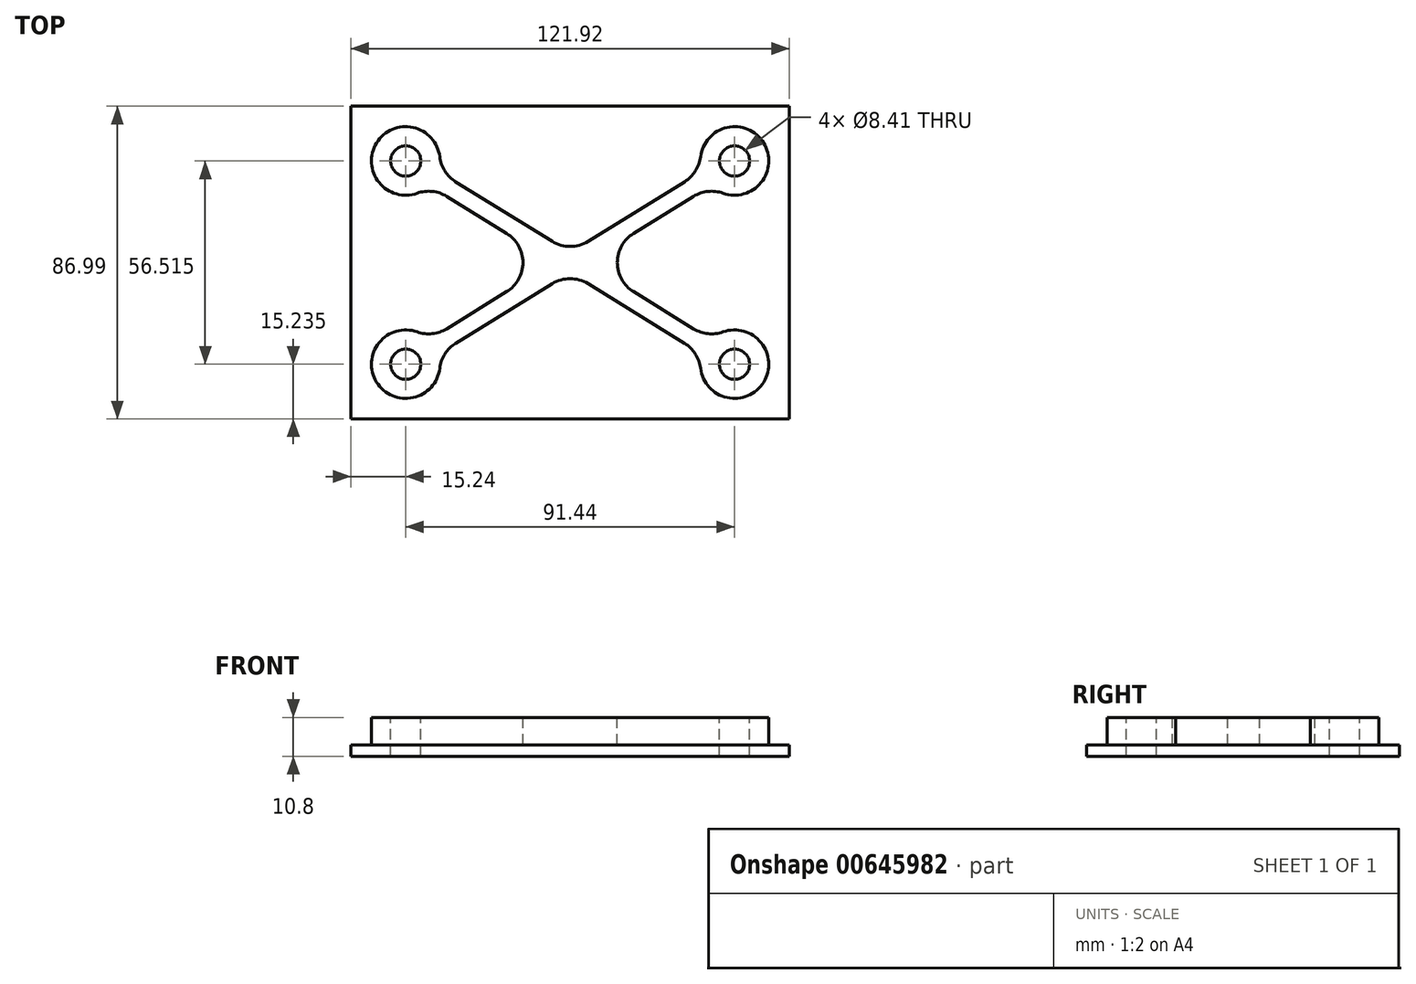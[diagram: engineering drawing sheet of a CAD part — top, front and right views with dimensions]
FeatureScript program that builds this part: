
annotation { "Feature Type Name" : "Feature", "Feature Type Description" : "" }
export const myFeature = defineFeature(function(context is Context, id is Id, definition is map)
    precondition{}
    {
        {
            var Q0;
            Q0=qCreatedBy(makeId("Top.planeOp"),FACE);
            var sketch = newSketch(context, id + "F0", { "sketchPlane" : qUnion([Q0])});
            skCircle(sketch, "E0", {"center": v(0, 0) * mm, "radius": 15.24 * mm});
            skCircle(sketch, "E1", {"center": v(-91.44, 0) * mm, "radius": 15.24 * mm});
            skCircle(sketch, "E2", {"center": v(0, -56.52) * mm, "radius": 15.24 * mm});
            skCircle(sketch, "E3", {"center": v(-91.44, -56.52) * mm, "radius": 15.24 * mm});
            skLineSegment(sketch, "E4", {"start": v(-106.68, 0) * mm, "end": v(-106.68, -56.52) * mm});
            skLineSegment(sketch, "E5", {"start": v(-91.44, -71.76) * mm, "end": v(0, -71.76) * mm});
            skLineSegment(sketch, "E6", {"start": v(15.24, 0) * mm, "end": v(15.24, -56.52) * mm});
            skLineSegment(sketch, "E7", {"start": v(0, 15.24) * mm, "end": v(-91.44, 15.24) * mm});
            skLineSegment(sketch, "E8", {"start": v(0, 15.24) * mm, "end": v(15.24, 15.24) * mm});
            skLineSegment(sketch, "E9", {"start": v(15.24, 0) * mm, "end": v(15.24, 15.24) * mm});
            skLineSegment(sketch, "E10", {"start": v(-91.44, 15.24) * mm, "end": v(-106.68, 15.24) * mm});
            skLineSegment(sketch, "E11", {"start": v(-106.68, 0) * mm, "end": v(-106.68, 15.24) * mm});
            skLineSegment(sketch, "E12", {"start": v(15.24, -56.52) * mm, "end": v(15.24, -71.76) * mm});
            skLineSegment(sketch, "E13", {"start": v(0, -71.76) * mm, "end": v(15.24, -71.76) * mm});
            skLineSegment(sketch, "E14", {"start": v(-106.68, -56.52) * mm, "end": v(-106.68, -71.76) * mm});
            skLineSegment(sketch, "E15", {"start": v(-91.44, -71.76) * mm, "end": v(-106.68, -71.76) * mm});
            skSolve(sketch);
        }
        {
            var Q0;
            {var subQ0=sQuery(id+"F0.wireOp",EDGE,"E4");Q0=makeQuery(id+"F0.imprint","IMPRINT",FACE,{"disambiguationData":[TD([[makeQuery(id+"F0.imprint","IMPRINT",EDGE,{"derivedFrom":subQ0}),1.0]])]});}
            var Q1;
            {var subQ0=sQuery(id+"F0.wireOp",EDGE,"E3");var subQ1=makeQuery(id+"F0.imprint","INTERSECT",VERTEX,{"derivedFrom":[subQ0,sQuery(id+"F0.wireOp",EDGE,"E4")]});Q1=makeQuery(id+"F0.imprint","IMPRINT",FACE,{"disambiguationData":[TD([[makeQuery(id+"F0.imprint","IMPRINT",EDGE,{"disambiguationData":[TD([[subQ1,-1.0]])],"derivedFrom":subQ0}),1.0]])]});}
            var Q2;
            {var subQ0=sQuery(id+"F0.wireOp",EDGE,"E1");var subQ1=makeQuery(id+"F0.imprint","INTERSECT",VERTEX,{"derivedFrom":[subQ0,sQuery(id+"F0.wireOp",EDGE,"E4")]});Q2=makeQuery(id+"F0.imprint","IMPRINT",FACE,{"disambiguationData":[TD([[makeQuery(id+"F0.imprint","IMPRINT",EDGE,{"disambiguationData":[TD([[subQ1,1.0]])],"derivedFrom":subQ0}),1.0]])]});}
            var Q3;
            {var subQ0=sQuery(id+"F0.wireOp",EDGE,"E0");var subQ1=makeQuery(id+"F0.imprint","INTERSECT",VERTEX,{"derivedFrom":[subQ0,sQuery(id+"F0.wireOp",EDGE,"E6")]});Q3=makeQuery(id+"F0.imprint","IMPRINT",FACE,{"disambiguationData":[TD([[makeQuery(id+"F0.imprint","IMPRINT",EDGE,{"disambiguationData":[TD([[subQ1,-1.0]])],"derivedFrom":subQ0}),1.0]])]});}
            var Q4;
            {var subQ0=sQuery(id+"F0.wireOp",EDGE,"E2");var subQ1=makeQuery(id+"F0.imprint","INTERSECT",VERTEX,{"derivedFrom":[subQ0,sQuery(id+"F0.wireOp",EDGE,"E5")]});Q4=makeQuery(id+"F0.imprint","IMPRINT",FACE,{"disambiguationData":[TD([[makeQuery(id+"F0.imprint","IMPRINT",EDGE,{"disambiguationData":[TD([[subQ1,1.0]])],"derivedFrom":subQ0}),1.0]])]});}
            var Q5;
            {var subQ2=sQuery(id+"F0.wireOp",EDGE,"E12");Q5=makeQuery(id+"F0.imprint","IMPRINT",FACE,{"disambiguationData":[TD([[makeQuery(id+"F0.imprint","IMPRINT",EDGE,{"derivedFrom":subQ2}),-1.0]])]});}
            var Q6;
            {var subQ0=sQuery(id+"F0.wireOp",EDGE,"E14");Q6=makeQuery(id+"F0.imprint","IMPRINT",FACE,{"disambiguationData":[TD([[makeQuery(id+"F0.imprint","IMPRINT",EDGE,{"derivedFrom":subQ0}),1.0]])]});}
            var Q7;
            {var subQ2=sQuery(id+"F0.wireOp",EDGE,"E10");Q7=makeQuery(id+"F0.imprint","IMPRINT",FACE,{"disambiguationData":[TD([[makeQuery(id+"F0.imprint","IMPRINT",EDGE,{"derivedFrom":subQ2}),1.0]])]});}
            var Q8;
            {var subQ2=sQuery(id+"F0.wireOp",EDGE,"E8");Q8=makeQuery(id+"F0.imprint","IMPRINT",FACE,{"disambiguationData":[TD([[makeQuery(id+"F0.imprint","IMPRINT",EDGE,{"derivedFrom":subQ2}),-1.0]])]});}
            extrude(context, id + "F1", {"entities" : qUnion([Q0, Q1, Q2, Q3, Q4, Q5, Q6, Q7, Q8]), "oppositeDirection" : true, "depth" : 3.17 * mm, "offsetDistance" : 25.4 * mm});
        }
        {
            var Q0;
            {var subQ0=sQuery(id+"F0.wireOp",EDGE,"E4");Q0=makeQuery(id+"F0.imprint","IMPRINT",FACE,{"disambiguationData":[TD([[makeQuery(id+"F0.imprint","IMPRINT",EDGE,{"derivedFrom":subQ0}),1.0]])]});}
            var sketch = newSketch(context, id + "F2", { "sketchPlane" : qUnion([Q0])});
            skLineSegment(sketch, "E16", {"start": v(-91.44, 0) * mm, "end": v(0, -56.52) * mm, "construction": true});
            skLineSegment(sketch, "E17", {"start": v(0, 0) * mm, "end": v(-91.44, -56.52) * mm, "construction": true});
            skLineSegment(sketch, "E18", {"start": v(-84.85, -6.87) * mm, "end": v(-50.25, -28.26) * mm});
            skLineSegment(sketch, "E19", {"start": v(-82.34, -2.82) * mm, "end": v(-45.72, -25.46) * mm});
            skLineSegment(sketch, "E20", {"start": v(-6.6, -6.87) * mm, "end": v(-41.2, -28.26) * mm});
            skLineSegment(sketch, "E21", {"start": v(-9.1, -2.82) * mm, "end": v(-45.72, -25.46) * mm});
            skLineSegment(sketch, "E22.trimOffspring", {"start": v(-50.25, -28.26) * mm, "end": v(-84.85, -49.64) * mm});
            skLineSegment(sketch, "E23.trimOffspring", {"start": v(-45.72, -31.06) * mm, "end": v(-9.1, -53.7) * mm});
            skLineSegment(sketch, "E24.trimOffspring", {"start": v(-45.72, -31.06) * mm, "end": v(-82.34, -53.7) * mm});
            skLineSegment(sketch, "E25.trimOffspring", {"start": v(-41.2, -28.26) * mm, "end": v(-6.6, -49.64) * mm});
            skArc(sketch, "E26", {"start": v(-82.34, -2.82) * mm, "mid": v(-99.54, 5) * mm, "end": v(-84.85, -6.87) * mm});
            skArc(sketch, "E27", {"start": v(-84.85, -49.64) * mm, "mid": v(-99.54, -61.52) * mm, "end": v(-82.34, -53.7) * mm});
            skArc(sketch, "E28", {"start": v(-9.1, -53.7) * mm, "mid": v(8.1, -61.52) * mm, "end": v(-6.6, -49.64) * mm});
            skArc(sketch, "E29", {"start": v(-6.6, -6.87) * mm, "mid": v(8.1, 5) * mm, "end": v(-9.1, -2.82) * mm});
            skSolve(sketch);
        }
        {
            var Q0;
            {var subQ0=sQuery(id+"F2.wireOp",EDGE,"E29");Q0=makeQuery(id+"F2.imprint","IMPRINT",FACE,{"disambiguationData":[TD([[makeQuery(id+"F2.imprint","IMPRINT",EDGE,{"derivedFrom":subQ0}),1.0]])]});}
            var Q1;
            {var subQ0=sQuery(id+"F2.wireOp",EDGE,"E28");Q1=makeQuery(id+"F2.imprint","IMPRINT",FACE,{"disambiguationData":[TD([[makeQuery(id+"F2.imprint","IMPRINT",EDGE,{"derivedFrom":subQ0}),1.0]])]});}
            var Q2;
            {var subQ0=sQuery(id+"F2.wireOp",EDGE,"E27");Q2=makeQuery(id+"F2.imprint","IMPRINT",FACE,{"disambiguationData":[TD([[makeQuery(id+"F2.imprint","IMPRINT",EDGE,{"derivedFrom":subQ0}),1.0]])]});}
            var Q3;
            {var subQ0=sQuery(id+"F2.wireOp",EDGE,"E26");Q3=makeQuery(id+"F2.imprint","IMPRINT",FACE,{"disambiguationData":[TD([[makeQuery(id+"F2.imprint","IMPRINT",EDGE,{"derivedFrom":subQ0}),1.0]])]});}
            var Q4;
            {var subQ1=sQuery(id+"F2.wireOp",EDGE,"E18");Q4=makeQuery(id+"F2.imprint","IMPRINT",FACE,{"disambiguationData":[TD([[makeQuery(id+"F2.imprint","IMPRINT",EDGE,{"derivedFrom":subQ1}),1.0]])]});}
            var Q5;
            {var subQ21=sQuery(id+"F2.wireOp",EDGE,"E22.trimOffspring");var subQ22=sQuery(id+"F2.wireOp",EDGE,"E18");var subQ23=makeQuery(id+"F2.imprint","INTERSECT",VERTEX,{"derivedFrom":[subQ22,subQ21]});Q5=makeQuery(id+"F2.imprint","IMPRINT",FACE,{"disambiguationData":[TD([[makeQuery(id+"F2.imprint","IMPRINT",EDGE,{"disambiguationData":[TD([[subQ23,1.0]])],"derivedFrom":subQ22}),1.0]])]});}
            extrude(context, id + "F3", {"entities" : qUnion([Q0, Q1, Q2, Q3, Q4, Q5]), "operationType" : NewBodyOperationType.ADD, "depth" : 7.62 * mm, "offsetDistance" : 25.4 * mm});
        }
        {
            var Q0;
            Q0=makeQuery(id+"F3.opExtrude","SWEPT_EDGE",EDGE,{"disambiguationData":[OSD([sQuery(id+"F2.wireOp",EDGE,"E23.trimOffspring"),sQuery(id+"F2.wireOp",EDGE,"E24.trimOffspring")])]});
            var Q1;
            Q1=makeQuery(id+"F3.opExtrude","SWEPT_EDGE",EDGE,{"disambiguationData":[OSD([sQuery(id+"F0.wireOp",EDGE,"E3"),sQuery(id+"F2.wireOp",EDGE,"E24.trimOffspring"),sQuery(id+"F2.wireOp",EDGE,"E27")])]});
            var Q2;
            Q2=makeQuery(id+"F3.opExtrude","SWEPT_EDGE",EDGE,{"disambiguationData":[OSD([sQuery(id+"F0.wireOp",EDGE,"E2"),sQuery(id+"F2.wireOp",EDGE,"E23.trimOffspring"),sQuery(id+"F2.wireOp",EDGE,"E28")])]});
            var Q3;
            Q3=makeQuery(id+"F3.opExtrude","SWEPT_EDGE",EDGE,{"disambiguationData":[OSD([sQuery(id+"F0.wireOp",EDGE,"E0"),sQuery(id+"F2.wireOp",EDGE,"E20"),sQuery(id+"F2.wireOp",EDGE,"E29")])]});
            var Q4;
            Q4=makeQuery(id+"F3.opExtrude","SWEPT_EDGE",EDGE,{"disambiguationData":[OSD([sQuery(id+"F0.wireOp",EDGE,"E3"),sQuery(id+"F2.wireOp",EDGE,"E22.trimOffspring"),sQuery(id+"F2.wireOp",EDGE,"E27")])]});
            var Q5;
            Q5=makeQuery(id+"F3.opExtrude","SWEPT_EDGE",EDGE,{"disambiguationData":[OSD([sQuery(id+"F2.wireOp",EDGE,"E18"),sQuery(id+"F2.wireOp",EDGE,"E22.trimOffspring")])]});
            var Q6;
            Q6=makeQuery(id+"F3.opExtrude","SWEPT_EDGE",EDGE,{"disambiguationData":[OSD([sQuery(id+"F0.wireOp",EDGE,"E1"),sQuery(id+"F2.wireOp",EDGE,"E18"),sQuery(id+"F2.wireOp",EDGE,"E26")])]});
            var Q7;
            Q7=makeQuery(id+"F3.opExtrude","SWEPT_EDGE",EDGE,{"disambiguationData":[OSD([sQuery(id+"F0.wireOp",EDGE,"E1"),sQuery(id+"F2.wireOp",EDGE,"E19"),sQuery(id+"F2.wireOp",EDGE,"E26")])]});
            var Q8;
            Q8=makeQuery(id+"F3.opExtrude","SWEPT_EDGE",EDGE,{"disambiguationData":[OSD([sQuery(id+"F2.wireOp",EDGE,"E19"),sQuery(id+"F2.wireOp",EDGE,"E21")])]});
            var Q9;
            Q9=makeQuery(id+"F3.opExtrude","SWEPT_EDGE",EDGE,{"disambiguationData":[OSD([sQuery(id+"F0.wireOp",EDGE,"E0"),sQuery(id+"F2.wireOp",EDGE,"E21"),sQuery(id+"F2.wireOp",EDGE,"E29")])]});
            var Q10;
            Q10=makeQuery(id+"F3.opExtrude","SWEPT_EDGE",EDGE,{"disambiguationData":[OSD([sQuery(id+"F2.wireOp",EDGE,"E20"),sQuery(id+"F2.wireOp",EDGE,"E25.trimOffspring")])]});
            var Q11;
            Q11=makeQuery(id+"F3.opExtrude","SWEPT_EDGE",EDGE,{"disambiguationData":[OSD([sQuery(id+"F0.wireOp",EDGE,"E2"),sQuery(id+"F2.wireOp",EDGE,"E25.trimOffspring"),sQuery(id+"F2.wireOp",EDGE,"E28")])]});
            fillet(context, id + "F4", {"entities" : qUnion([Q0, Q1, Q2, Q3, Q4, Q5, Q6, Q7, Q8, Q9, Q10, Q11]), "radius" : 9.52 * mm, "tangentPropagation" : true, "allowEdgeOverflow" : false});
        }
        {
            var Q0;
            Q0=makeQuery(id+"F3.opExtrude","CAP_FACE",FACE,{"disambiguationData":[OSD([sQuery(id+"F2.wireOp",EDGE,"E18"),sQuery(id+"F2.wireOp",EDGE,"E19"),sQuery(id+"F2.wireOp",EDGE,"E20"),sQuery(id+"F2.wireOp",EDGE,"E21"),sQuery(id+"F2.wireOp",EDGE,"E22.trimOffspring"),sQuery(id+"F2.wireOp",EDGE,"E23.trimOffspring"),sQuery(id+"F2.wireOp",EDGE,"E24.trimOffspring"),sQuery(id+"F2.wireOp",EDGE,"E25.trimOffspring"),sQuery(id+"F2.wireOp",EDGE,"E26"),sQuery(id+"F2.wireOp",EDGE,"E27"),sQuery(id+"F2.wireOp",EDGE,"E28"),sQuery(id+"F2.wireOp",EDGE,"E29")])],"isStart":false});
            var sketch = newSketch(context, id + "F5", { "sketchPlane" : qUnion([Q0])});
            skCircle(sketch, "E30", {"center": v(-91.44, -56.52) * mm, "radius": 4.2 * mm});
            skCircle(sketch, "E31", {"center": v(-91.44, 0) * mm, "radius": 4.2 * mm});
            skCircle(sketch, "E32", {"center": v(0, 0) * mm, "radius": 4.2 * mm});
            skCircle(sketch, "E33", {"center": v(0, -56.52) * mm, "radius": 4.2 * mm});
            skSolve(sketch);
        }
        {
            var Q0;
            Q0=makeQuery(id+"F5.imprint","IMPRINT",FACE,{"disambiguationData":[TD([[makeQuery(id+"F5.imprint","IMPRINT",EDGE,{"derivedFrom":sQuery(id+"F5.wireOp",EDGE,"E33")}),1.0]])]});
            var Q1;
            Q1=makeQuery(id+"F5.imprint","IMPRINT",FACE,{"disambiguationData":[TD([[makeQuery(id+"F5.imprint","IMPRINT",EDGE,{"derivedFrom":sQuery(id+"F5.wireOp",EDGE,"E30")}),1.0]])]});
            var Q2;
            Q2=makeQuery(id+"F5.imprint","IMPRINT",FACE,{"disambiguationData":[TD([[makeQuery(id+"F5.imprint","IMPRINT",EDGE,{"derivedFrom":sQuery(id+"F5.wireOp",EDGE,"E31")}),1.0]])]});
            var Q3;
            Q3=makeQuery(id+"F5.imprint","IMPRINT",FACE,{"disambiguationData":[TD([[makeQuery(id+"F5.imprint","IMPRINT",EDGE,{"derivedFrom":sQuery(id+"F5.wireOp",EDGE,"E32")}),1.0]])]});
            extrude(context, id + "F6", {"entities" : qUnion([Q0, Q1, Q2, Q3]), "operationType" : NewBodyOperationType.REMOVE, "endBound" : BoundingType.THROUGH_ALL, "oppositeDirection" : true, "depth" : 25.4 * mm, "offsetDistance" : 25.4 * mm});
        }
    });
